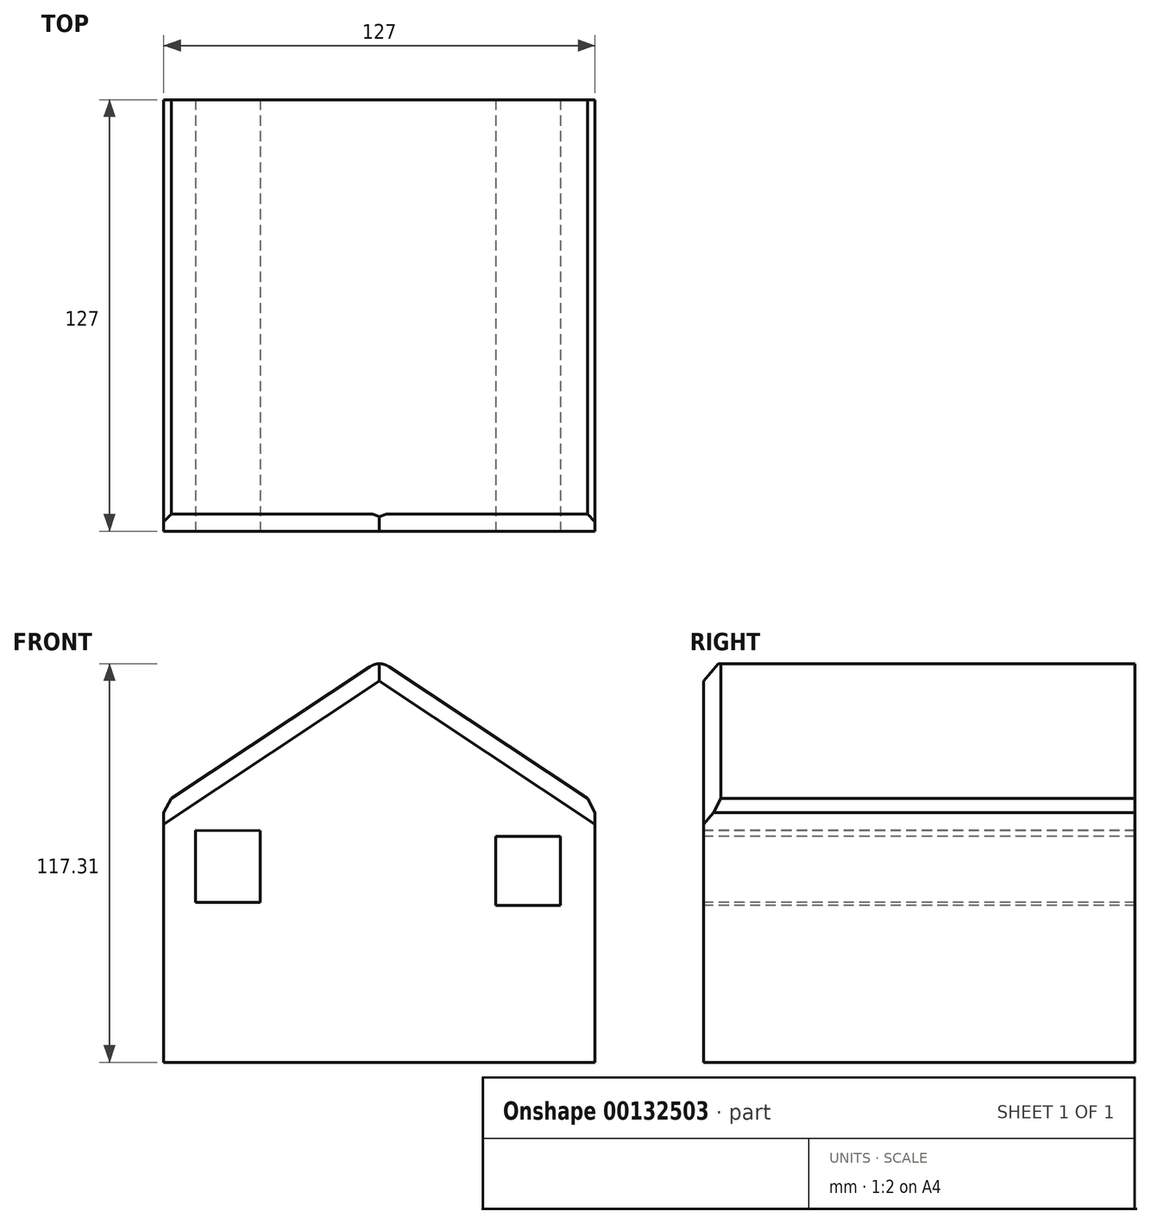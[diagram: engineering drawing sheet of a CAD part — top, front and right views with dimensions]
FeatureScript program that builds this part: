
annotation { "Feature Type Name" : "Feature", "Feature Type Description" : "" }
export const myFeature = defineFeature(function(context is Context, id is Id, definition is map)
    precondition{}
    {
        {
            var Q0;
            Q0=qCreatedBy(makeId("Front.planeOp"),FACE);
            var sketch = newSketch(context, id + "F0", { "sketchPlane" : qUnion([Q0])});
            skLineSegment(sketch, "E0", {"start": v(-63.5, 0) * mm, "end": v(-63.5, -76.2) * mm});
            skLineSegment(sketch, "E1", {"start": v(-63.5, -76.2) * mm, "end": v(63.5, -76.2) * mm});
            skLineSegment(sketch, "E2", {"start": v(63.5, -76.2) * mm, "end": v(63.5, 0) * mm});
            skLineSegment(sketch, "E3", {"start": v(63.5, 0) * mm, "end": v(0, 42.12) * mm});
            skLineSegment(sketch, "E4", {"start": v(0, 42.12) * mm, "end": v(-63.5, 0) * mm});
            skLineSegment(sketch, "E5", {"start": v(63.5, 0) * mm, "end": v(-63.5, 0) * mm});
            skLineSegment(sketch, "E6", {"start": v(-54.12, -7.9) * mm, "end": v(-54.12, -29.08) * mm});
            skLineSegment(sketch, "E7", {"start": v(-54.12, -29.08) * mm, "end": v(-35.07, -29.08) * mm});
            skLineSegment(sketch, "E8", {"start": v(-35.07, -29.08) * mm, "end": v(-35.07, -8.1) * mm});
            skLineSegment(sketch, "E9", {"start": v(-35.07, -8.1) * mm, "end": v(-54.12, -7.9) * mm});
            skLineSegment(sketch, "E10", {"start": v(34.2, -9.7) * mm, "end": v(34.2, -29.98) * mm});
            skLineSegment(sketch, "E11", {"start": v(34.2, -29.98) * mm, "end": v(53.24, -29.98) * mm});
            skLineSegment(sketch, "E12", {"start": v(53.24, -29.98) * mm, "end": v(53.24, -9.7) * mm});
            skLineSegment(sketch, "E13", {"start": v(53.24, -9.7) * mm, "end": v(34.2, -9.7) * mm});
            skLineSegment(sketch, "E14", {"start": v(-10.32, -38.1) * mm, "end": v(12.5, -38.34) * mm});
            skLineSegment(sketch, "E15", {"start": v(12.5, -38.34) * mm, "end": v(12.5, -76.2) * mm});
            skLineSegment(sketch, "E16", {"start": v(12.5, -76.2) * mm, "end": v(-10.73, -76.2) * mm});
            skLineSegment(sketch, "E17", {"start": v(-10.73, -76.2) * mm, "end": v(-10.32, -38.1) * mm});
            skSolve(sketch);
        }
        {
            var Q0;
            Q0 = qSketchRegion(id + "F0", true);
            extrude(context, id + "F1", {"entities" : qUnion([Q0]), "oppositeDirection" : true, "depth" : 127 * mm});
        }
        {
            var Q0;
            Q0=makeQuery(id+"F1.opExtrude","SWEPT_EDGE",EDGE,{"disambiguationData":[OSD([sQuery(id+"F0.wireOp",EDGE,"E0"),sQuery(id+"F0.wireOp",EDGE,"E4"),sQuery(id+"F0.wireOp",EDGE,"E5")])]});
            var Q1;
            Q1=makeQuery(id+"F1.opExtrude","SWEPT_EDGE",EDGE,{"disambiguationData":[OSD([sQuery(id+"F0.wireOp",EDGE,"E2"),sQuery(id+"F0.wireOp",EDGE,"E3"),sQuery(id+"F0.wireOp",EDGE,"E5")])]});
            var Q2;
            Q2=makeQuery(id+"F1.opExtrude","CAP_EDGE",EDGE,{"disambiguationData":[OSD([sQuery(id+"F0.wireOp",EDGE,"E3")])],"isStart":true});
            var Q3;
            Q3=makeQuery(id+"F1.opExtrude","CAP_EDGE",EDGE,{"disambiguationData":[OSD([sQuery(id+"F0.wireOp",EDGE,"E4")])],"isStart":true});
            chamfer(context, id + "F2", {"entities" : qUnion([Q0, Q1, Q2, Q3]), "width" : 5.08 * mm, "tangentPropagation" : true});
        }
        {
            var Q0;
            Q0=makeQuery(id+"F1.opExtrude","SWEPT_EDGE",EDGE,{"disambiguationData":[OSD([sQuery(id+"F0.wireOp",EDGE,"E3"),sQuery(id+"F0.wireOp",EDGE,"E4")])]});
            fillet(context, id + "F3", {"entities" : qUnion([Q0]), "radius" : 5.08 * mm, "tangentPropagation" : true, "allowEdgeOverflow" : false});
        }
    });
